FCSTD DOCUMENT  (FreeCAD 0.20R29603 (Git))
Label: 3d_printable_servo_piston
License: All rights reserved
LicenseURL: http://en.wikipedia.org/wiki/All_rights_reserved
objects: App::Part×3, Sketcher::SketchObject×1, PartDesign::Body×1, Spreadsheet::Sheet×1
note: 2 computed .brp shape members not serialized (recipe doc carries the construction recipe); baked Part::Feature solids carry a one-line shape summary decoded from their .brp

FEATURE [App::Part] Part  label="inside_threaded_gear"
  Origin = -> Origin
FEATURE [App::Part] Part001  label="Rod"
  Origin = -> Origin001
FEATURE [Sketcher::SketchObject] Sketch
  FullyConstrained = true
  MapMode = 5
  Support = -> [XY_Plane003]
FEATURE [PartDesign::Body] Body
  Group = -> [Sketch]
  Origin = -> Origin003
FEATURE [App::Part] Part002  label="PistonCasing"
  Group = -> [Body]
  Origin = -> Origin002
FEATURE [Spreadsheet::Sheet] Spreadsheet
  cells = A1=Piston parameters; C1=Printing parameters; F1=Servo motor parameters; A2=stroke_length; B2(stroke_length)==30mm; C2=printer_resolution; D2(printer_resolution)==0.4mm; F2=type; G2=sg90; A3=piston_rod_diameter; B3(piston_rod_diameter)==4mm; F3=servo_shaft_diameter; G3(servo_shaft_diameter)==4.9mm; A4=tooth_height; B4(tooth_heigh)==1mm; F4=servo_shaft_thread_diameter; A5=tooth_depth; B5(tooth_depth)==1mm; F5=servo_shaft_height; G5==3.5mm; A6=tooth_rear_height; B6(tooth_rear_height)==printer_resolution * 2 + tooth_depth; F6=servo_output_degrees; G6(servo_output_degrees)=180; A7=piston_bore_diameter; A9=Inner actuator gear; D9=Notes; A10=actuator_wall_thickness; B10(actuator_wall_thickness)==2mm; D10=These tolerances at resolution x 2; A11=actuator_height; B11(actuator_height)==stroke_length; D11=Could they be x 1?; A12=actuator_degrees_per_mm; B12(actuator_degrees_per_mm)==servo_output_degrees / stroke_length; D12=Experiment.; A13=actuator_revolutions_per_stroke; B13(actuator_revolutions_per_stroke)=0.5; A14=actuator_floor_thickness; B14(actuator_floor_thickness)==2mm; A15=actuator_inner_diameter; B15(actuator_inner_diameter)==piston_rod_diameter + printer_resolution * 2 + tooth_depth * 2; A16=actuator_outer_diameter; B16(actuator_outer_diameter)==actuator_inner_diameter + actuator_wall_thickness * 2; A17=actuator_total_height; B17(actuator_total_height)==actuator_height + actuator_floor_thickness; A19=Piston Casing; A20=casing_inner_diameter; B20(casing_inner_diameter)==actuator_outer_diameter + printer_resolution * 2; A21=casing_wall_thickness; B21(casing_wall_thickness)==2mm; A22=casing_outer_diameter; B22(casing_outer_diameter)==casing_inner_diameter + casing_wall_thickness * 2; A23=casing_inner_height; B23==actuator_total_height
